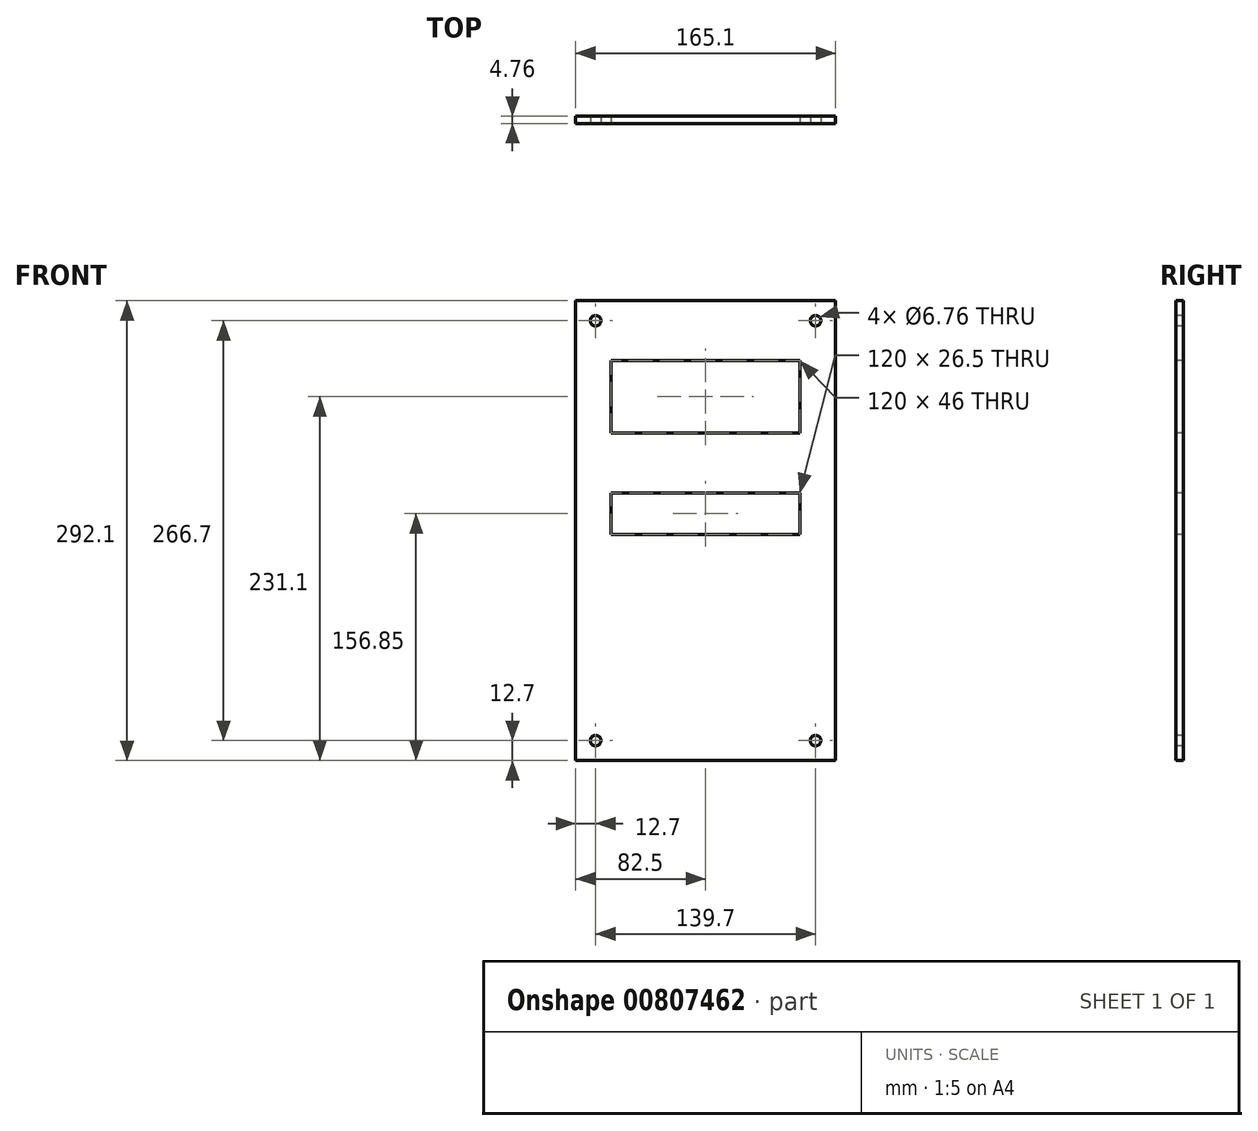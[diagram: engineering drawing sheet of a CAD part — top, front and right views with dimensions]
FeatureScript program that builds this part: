
annotation { "Feature Type Name" : "Feature", "Feature Type Description" : "" }
export const myFeature = defineFeature(function(context is Context, id is Id, definition is map)
    precondition{}
    {
        {
            var Q0;
            Q0=qCreatedBy(makeId("Front.planeOp"),FACE);
            var sketch = newSketch(context, id + "F0", { "sketchPlane" : qUnion([Q0])});
            skLineSegment(sketch, "E0.bottom", {"start": v(0, 0) * mm, "end": v(165.1, 0) * mm});
            skLineSegment(sketch, "E0.top", {"start": v(0, 292.1) * mm, "end": v(165.1, 292.1) * mm});
            skLineSegment(sketch, "E0.left", {"start": v(0, 0) * mm, "end": v(0, 292.1) * mm});
            skLineSegment(sketch, "E0.right", {"start": v(165.1, 0) * mm, "end": v(165.1, 292.1) * mm});
            skSolve(sketch);
        }
        {
            var Q0;
            Q0=makeQuery(id+"F0.imprint","IMPRINT",FACE,{"disambiguationData":[TD([[makeQuery(id+"F0.imprint","IMPRINT",EDGE,{"derivedFrom":sQuery(id+"F0.wireOp",EDGE,"E0.bottom")}),1.0]])]});
            extrude(context, id + "F1", {"entities" : qUnion([Q0]), "depth" : 4.76 * mm, "offsetDistance" : 25.4 * mm});
        }
        {
            var Q0;
            Q0=makeQuery(id+"F1.opExtrude","CAP_FACE",FACE,{"disambiguationData":[OSD([sQuery(id+"F0.wireOp",EDGE,"E0.bottom"),sQuery(id+"F0.wireOp",EDGE,"E0.top"),sQuery(id+"F0.wireOp",EDGE,"E0.left"),sQuery(id+"F0.wireOp",EDGE,"E0.right")])],"isStart":false});
            var sketch = newSketch(context, id + "F2", { "sketchPlane" : qUnion([Q0])});
            skPoint(sketch, "E1", {"position": v(12.7, 279.4) * mm});
            skLineSegment(sketch, "E2", {"start": v(82.55, 292.1) * mm, "end": v(82.55, 0) * mm});
            skLineSegment(sketch, "E3", {"start": v(0, 146.05) * mm, "end": v(165.1, 146.05) * mm});
            skPoint(sketch, "E4.MirrorP", {"position": v(152.4, 279.4) * mm});
            skPoint(sketch, "E5.MirrorP", {"position": v(12.7, 12.7) * mm});
            skPoint(sketch, "E6.MirrorP", {"position": v(152.4, 12.7) * mm});
            skSolve(sketch);
        }
        {
            var Q0;
            Q0=sQuery(id+"F2.wireOp",VERTEX,"E1");
            var Q1;
            Q1=sQuery(id+"F2.wireOp",VERTEX,"E4.MirrorP");
            var Q2;
            Q2=sQuery(id+"F2.wireOp",VERTEX,"E5.MirrorP");
            var Q3;
            Q3=sQuery(id+"F2.wireOp",VERTEX,"E6.MirrorP");
            var Q4;
            Q4=makeQuery(id+"F1.opExtrude","SWEPT_BODY",BODY,{"disambiguationData":[OSD([sQuery(id+"F0.wireOp",EDGE,"E0.bottom"),sQuery(id+"F0.wireOp",EDGE,"E0.top"),sQuery(id+"F0.wireOp",EDGE,"E0.left"),sQuery(id+"F0.wireOp",EDGE,"E0.right")])]});
            hole(context, id + "F3", {"style" : HoleStyle.SIMPLE, "endStyle" : HoleEndStyle.THROUGH, "standardTappedOrClearance" : lookupTablePath({ "standard" : "ANSI", "fit" : "Normal (ASME)", "size" : "1/4", "type" : "Clearance" }), "standardBlindInLast" : lookupTablePath({ "fit" : "Free", "standard" : "ANSI", "size" : "1/4", "type" : "Clearance" }), "holeDiameter" : 6.76 * mm, "majorDiameter" : 6.35 * mm, "isTappedThrough" : true, "tappedDepth" : 25.4 * mm, "tapClearance" : 3, "locations" : qUnion([Q0, Q1, Q2, Q3]), "scope" : qUnion([Q4])});
        }
        {
            var Q0;
            Q0=makeQuery(id+"F1.opExtrude","CAP_FACE",FACE,{"disambiguationData":[OSD([sQuery(id+"F0.wireOp",EDGE,"E0.bottom"),sQuery(id+"F0.wireOp",EDGE,"E0.top"),sQuery(id+"F0.wireOp",EDGE,"E0.left"),sQuery(id+"F0.wireOp",EDGE,"E0.right")])],"isStart":false});
            var sketch = newSketch(context, id + "F4", { "sketchPlane" : qUnion([Q0])});
            skLineSegment(sketch, "E7.bottom", {"start": v(22.5, 254.1) * mm, "end": v(142.5, 254.1) * mm});
            skLineSegment(sketch, "E7.top", {"start": v(22.5, 208.1) * mm, "end": v(142.5, 208.1) * mm});
            skLineSegment(sketch, "E7.left", {"start": v(22.5, 254.1) * mm, "end": v(22.5, 208.1) * mm});
            skLineSegment(sketch, "E7.right", {"start": v(142.5, 254.1) * mm, "end": v(142.5, 208.1) * mm});
            skLineSegment(sketch, "E8.bottom", {"start": v(22.5, 170.1) * mm, "end": v(142.5, 170.1) * mm});
            skLineSegment(sketch, "E8.top", {"start": v(22.5, 143.6) * mm, "end": v(142.5, 143.6) * mm});
            skLineSegment(sketch, "E8.left", {"start": v(22.5, 170.1) * mm, "end": v(22.5, 143.6) * mm});
            skLineSegment(sketch, "E8.right", {"start": v(142.5, 170.1) * mm, "end": v(142.5, 143.6) * mm});
            skSolve(sketch);
        }
        {
            var Q0;
            Q0=makeQuery(id+"F4.imprint","IMPRINT",FACE,{"disambiguationData":[TD([[makeQuery(id+"F4.imprint","IMPRINT",EDGE,{"derivedFrom":sQuery(id+"F4.wireOp",EDGE,"E7.bottom")}),-1.0]])]});
            var Q1;
            Q1=makeQuery(id+"F4.imprint","IMPRINT",FACE,{"disambiguationData":[TD([[makeQuery(id+"F4.imprint","IMPRINT",EDGE,{"derivedFrom":sQuery(id+"F4.wireOp",EDGE,"E8.bottom")}),-1.0]])]});
            extrude(context, id + "F5", {"entities" : qUnion([Q0, Q1]), "operationType" : NewBodyOperationType.REMOVE, "endBound" : BoundingType.THROUGH_ALL, "oppositeDirection" : true, "depth" : 25.4 * mm, "offsetDistance" : 25.4 * mm});
        }
    });
